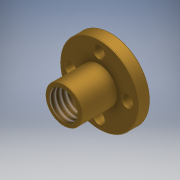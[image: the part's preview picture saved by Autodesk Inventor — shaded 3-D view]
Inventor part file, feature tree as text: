
AUTODESK INVENTOR PART (.ipt)
format: ipt  version: 2017.3 (Build 213256000, 256)  size: 179,200 bytes
history: native  units: mm
features: sketch x2, revolve x1, extrude x1, chamfer x1, fillet x1, thread x1
ambient origin geometry x8: Origin, YZ Plane, XZ Plane, XY Plane, X Axis, Y Axis, Z Axis, Center Point
bodies: Solid1 (feature_tree)
feature tree (7):
  revolve  "Revolution1"  [1 undecoded]
  extrude  "Extrusion1"  Depth=11.0mm
  chamfer  "Chamfer1"  Distance=4.0mm
  fillet  "Fillet1"  Radius=5.15mm
  thread  "Thread1"  [1 undecoded]
  sketch  "Sketch1"  dims[d1=3.5mm d2=1.5mm]
  sketch  "Sketch2"  dims[d3=15.0mm d4=11.0mm d5=4.0mm d6=5.15mm d7=90.0deg d8=16.0mm d9=3.5mm d10=10.0mm d11=0.0mm d12=0.25mm d13=2.0mm d14=45.0deg d15=0.25mm d16=10.0mm d17=0.0mm]
note: 2 required parameter values undecoded (feature->parameter linkage not recoverable at this tier; creation-order binding heuristic only, values carry confidence <= 0.55)